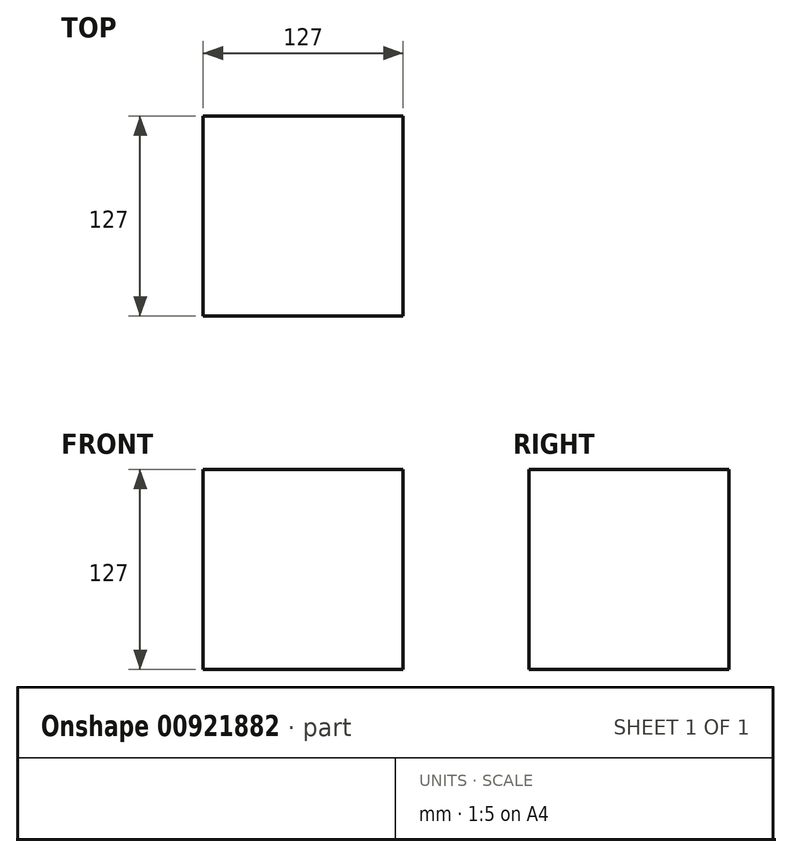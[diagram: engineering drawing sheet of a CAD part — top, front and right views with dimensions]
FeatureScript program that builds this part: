
annotation { "Feature Type Name" : "Feature", "Feature Type Description" : "" }
export const myFeature = defineFeature(function(context is Context, id is Id, definition is map)
    precondition{}
    {
        {
            var Q0;
            Q0=qCreatedBy(makeId("Front.planeOp"),FACE);
            var sketch = newSketch(context, id + "F0", { "sketchPlane" : qUnion([Q0])});
            skLineSegment(sketch, "E0.bottom", {"start": v(-86.48, 105.7) * mm, "end": v(40.52, 105.7) * mm});
            skLineSegment(sketch, "E0.top", {"start": v(-86.48, -21.3) * mm, "end": v(40.52, -21.3) * mm});
            skLineSegment(sketch, "E0.left", {"start": v(-86.48, 105.7) * mm, "end": v(-86.48, -21.3) * mm});
            skLineSegment(sketch, "E0.right", {"start": v(40.52, 105.7) * mm, "end": v(40.52, -21.3) * mm});
            skSolve(sketch);
        }
        {
            var Q0;
            Q0=makeQuery(id+"F0.imprint","IMPRINT",FACE,{"disambiguationData":[TD([[makeQuery(id+"F0.imprint","IMPRINT",EDGE,{"derivedFrom":sQuery(id+"F0.wireOp",EDGE,"E0.bottom")}),-1.0]])]});
            extrude(context, id + "F1", {"entities" : qUnion([Q0]), "depth" : 127 * mm, "offsetDistance" : 25.4 * mm});
        }
    });
